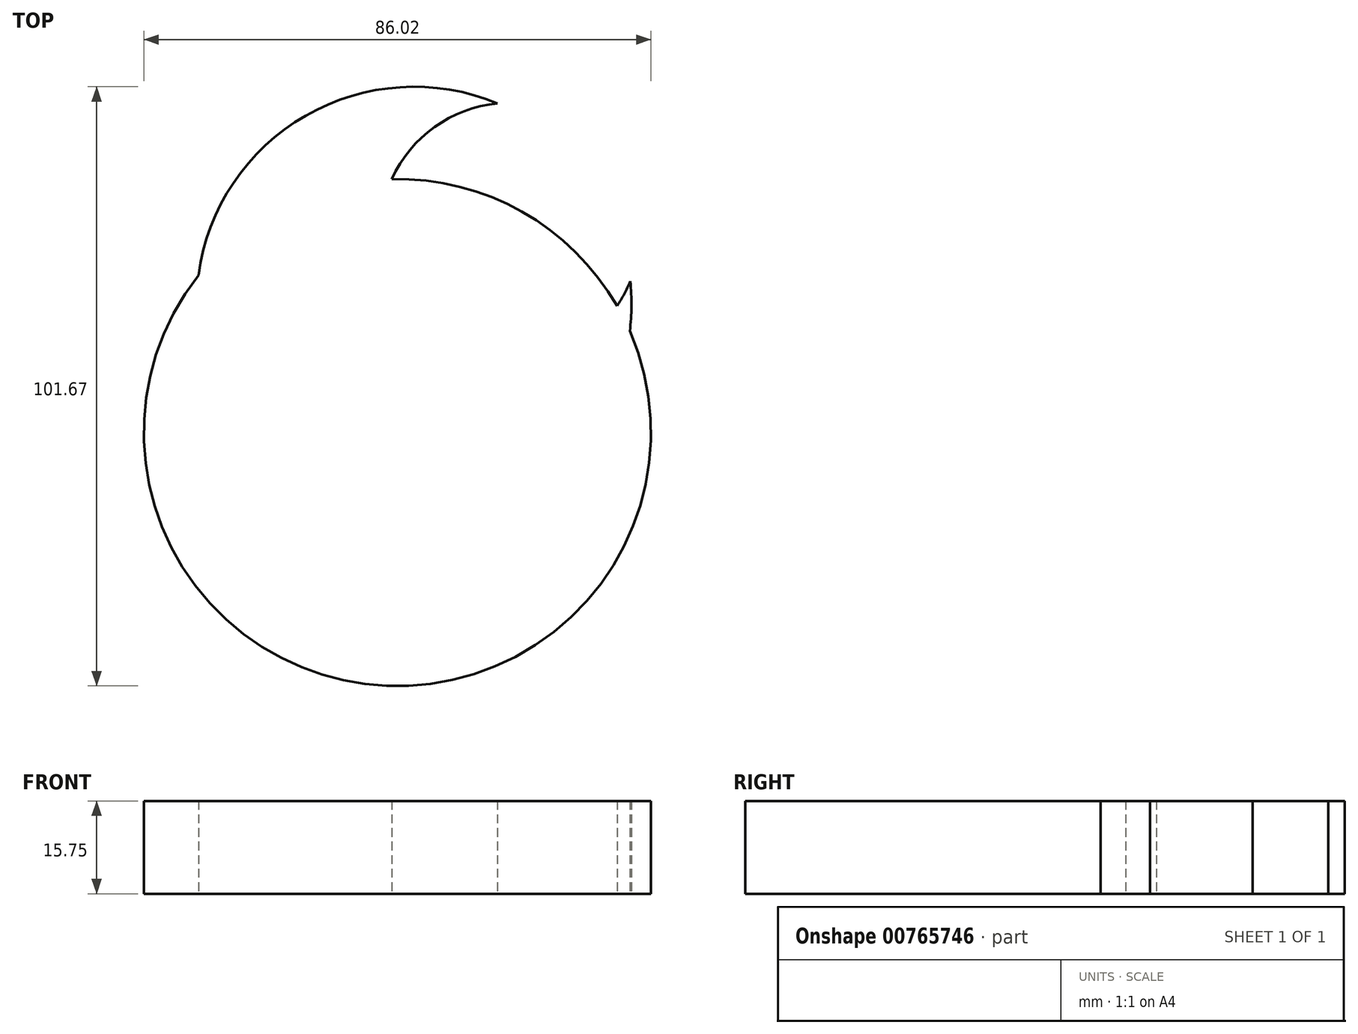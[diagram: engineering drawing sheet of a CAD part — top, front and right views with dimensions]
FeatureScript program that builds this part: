
annotation { "Feature Type Name" : "Feature", "Feature Type Description" : "" }
export const myFeature = defineFeature(function(context is Context, id is Id, definition is map)
    precondition{}
    {
        {
            var Q0;
            Q0=qCreatedBy(makeId("Top.planeOp"),FACE);
            var sketch = newSketch(context, id + "F0", { "sketchPlane" : qUnion([Q0])});
            skCircle(sketch, "E0", {"center": v(0, 0) * mm, "radius": 43 * mm});
            skSolve(sketch);
        }
        {
            var Q0;
            Q0=makeQuery(id+"F0.imprint","IMPRINT",FACE,{"disambiguationData":[TD([[makeQuery(id+"F0.imprint","IMPRINT",EDGE,{"derivedFrom":sQuery(id+"F0.wireOp",EDGE,"E0")}),1.0]])]});
            extrude(context, id + "F1", {"entities" : qUnion([Q0]), "depth" : 15.75 * mm, "offsetDistance" : 25.4 * mm});
        }
        {
            var Q0;
            Q0=qCreatedBy(makeId("Top.planeOp"),FACE);
            var sketch = newSketch(context, id + "F2", { "sketchPlane" : qUnion([Q0])});
            skCircle(sketch, "E1", {"center": v(2.82, 21.78) * mm, "radius": 36.88 * mm});
            skCircle(sketch, "E2", {"center": v(19.11, 33.93) * mm, "radius": 22 * mm});
            skSolve(sketch);
        }
        {
            var Q0;
            {var subQ0=sQuery(id+"F2.wireOp",EDGE,"E2");var subQ1=sQuery(id+"F2.wireOp",EDGE,"E1");var subQ2=makeQuery(id+"F2.imprint","INTERSECT",VERTEX,{"disambiguationData":[OD(0.0)],"derivedFrom":[subQ1,subQ0]});Q0=makeQuery(id+"F2.imprint","IMPRINT",FACE,{"disambiguationData":[TD([[makeQuery(id+"F2.imprint","IMPRINT",EDGE,{"disambiguationData":[TD([[subQ2,-1.0]])],"derivedFrom":subQ1}),1.0]])]});}
            extrude(context, id + "F3", {"entities" : qUnion([Q0]), "operationType" : NewBodyOperationType.ADD, "depth" : 15.75 * mm, "offsetDistance" : 25.4 * mm});
        }
    });
